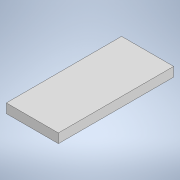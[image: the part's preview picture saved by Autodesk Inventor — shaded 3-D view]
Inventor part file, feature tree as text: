
AUTODESK INVENTOR PART (.ipt)
format: ipt  version: 2021 (Build 250183000, 183)  size: 89,088 bytes
history: native  units: mm
features: extrude x1, sketch x1
ambient origin geometry x8: Origin, YZ Plane, XZ Plane, XY Plane, X Axis, Y Axis, Z Axis, Center Point
bodies: Solid1 (feature_tree)
feature tree (2):
  extrude  "Extrusion1"  Depth=28.0mm
  sketch  "Sketch1"  dims[d0=5.0mm d1=28.0mm d2=62.0mm d3=0.0mm]
